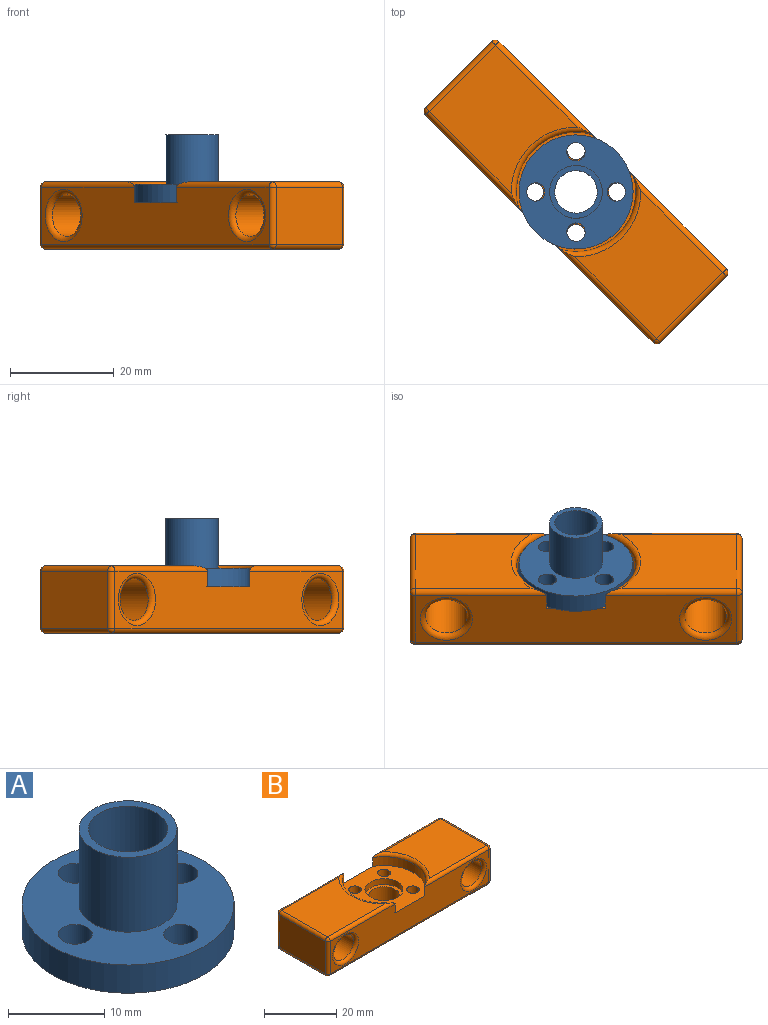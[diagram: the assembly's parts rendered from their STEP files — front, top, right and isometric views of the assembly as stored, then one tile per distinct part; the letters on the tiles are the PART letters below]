
ASSEMBLY  parts=2 mates=2
PART A: 12 faces, bbox 22x22x15.1 mm
  f0: cylinder r=1.77mm len=3.58mm, axis (0,0,-1), area 39.8mm2, adj f6,f7
  f1: cylinder r=1.77mm len=3.58mm, axis (0,0,-1), area 39.8mm2, adj f6,f7
  f2: cylinder r=1.77mm len=3.58mm, axis (0,0,-1), area 39.8mm2, adj f6,f7
  f3: cylinder r=1.77mm len=3.58mm, axis (0,0,-1), area 39.8mm2, adj f6,f7
  f4: cylinder r=4.1mm len=15.08mm, axis (0,0,-1), area 388.5mm2, adj f9,f11
  f5: cylinder r=11mm len=22mm, axis (0,0,-1), area 247.4mm2, adj f6,f7
  f6: plane 22x22mm, normal (0,0,1), area 259.5mm2, adj f0,f1,f2,f3,f5,f10
  f7: plane 22x22mm, normal (0,0,-1), area 245.7mm2, adj f0,f1,f2,f3,f5,f8
  f8: cylinder r=5.5mm len=11mm, axis (0,0,1), area 69.1mm2, adj f7,f9
  f9: plane 11x11mm, normal (0,0,-1), area 42.2mm2, adj f4,f8
  f10: cylinder r=5.08mm len=10.17mm, axis (0,0,-1), area 303.5mm2, adj f6,f11
  f11: plane 10.17x10.17mm, normal (0,0,1), area 28.4mm2, adj f4,f10
PART B: 75 faces, bbox 64x24.9x13 mm
  f0: cylinder r=4.25mm len=8.5mm, axis (0,0,1), area 186.9mm2, adj f4,f46
  f1: plane 22.33x18mm, normal (0,0,1), area 354.3mm2, adj f35,f36,f38,f40
  f2: plane 62x11mm, normal (0,-1,0), area 487.7mm2, adj f10,f11,f12,f22,f27,f32,f37,f40
  f3: plane 18x11mm, normal (-1,0,0), area 198mm2, adj f20,f21,f26,f27
  f4: plane 62x18mm, normal (0,0,-1), area 934.6mm2, adj f0,f25,f26,f31,f32,f47,f48,f49
  f5: plane 18x11mm, normal (1,0,0), area 198mm2, adj f30,f31,f36,f37
  f6: cylinder r=4.05mm len=18mm, axis (0,1,0), area 458mm2, adj f41,f43
  f7: plane 22.33x18mm, normal (0,0,1), area 354.3mm2, adj f17,f19,f21,f22
  f8: cylinder r=4.05mm len=18mm, axis (0,1,0), area 458mm2, adj f42,f44
  f9: plane 62x11mm, normal (0,1,0), area 487.7mm2, adj f10,f11,f12,f17,f20,f25,f30,f35
  f10: cylinder r=11.5mm len=20mm, axis (0,0,1), area 72.7mm2, adj f2,f9,f12,f38
  f11: cylinder r=11.5mm len=20mm, axis (0,0,1), area 72.7mm2, adj f2,f9,f12,f19
  f12: plane 23x20mm, normal (0,0,1), area 267.4mm2, adj f2,f9,f10,f11,f13,f14,f15,f16
  f13: cylinder r=1.75mm len=6mm, axis (0,0,1), area 66mm2, adj f12,f60
  f14: cylinder r=1.75mm len=6mm, axis (0,0,1), area 66mm2, adj f12,f74
  f15: cylinder r=1.75mm len=6mm, axis (0,0,1), area 66mm2, adj f12,f67
  f16: cylinder r=1.75mm len=6mm, axis (0,0,1), area 66mm2, adj f12,f53
  f17: cylinder r=1mm len=25.32mm, axis (-1,0,0), area 37.9mm2, adj f7,f9,f18,f19
  f18: sphere r=1mm, area 1.6mm2, adj f17,f20,f21
  f19: torus R=12.5mm, axis (0,0,1), area 35.5mm2, adj f7,f11,f17,f22
  f20: cylinder r=1mm len=11mm, axis (0,0,-1), area 17.3mm2, adj f3,f9,f18,f23
  f21: cylinder r=1mm len=18mm, axis (0,1,0), area 28.3mm2, adj f3,f7,f18,f24
  f22: cylinder r=1mm len=25.32mm, axis (1,0,0), area 37.9mm2, adj f2,f7,f19,f24
  f23: sphere r=1mm, area 1.6mm2, adj f20,f25,f26
  f24: sphere r=1mm, area 1.6mm2, adj f21,f22,f27
  f25: cylinder r=1mm len=62mm, axis (1,0,0), area 97.3mm2, adj f4,f9,f23,f28,f65,f66,f72,f73
  f26: cylinder r=1mm len=18mm, axis (0,-1,0), area 28.3mm2, adj f3,f4,f23,f29
  f27: cylinder r=1mm len=11mm, axis (0,0,1), area 17.3mm2, adj f2,f3,f24,f29
  f28: sphere r=1mm, area 1.6mm2, adj f25,f30,f31
  f29: sphere r=1mm, area 1.6mm2, adj f26,f27,f32
  f30: cylinder r=1mm len=11mm, axis (0,0,1), area 17.3mm2, adj f5,f9,f28,f33
  f31: cylinder r=1mm len=18mm, axis (0,1,0), area 28.3mm2, adj f4,f5,f28,f34
  f32: cylinder r=1mm len=62mm, axis (-1,0,0), area 97.3mm2, adj f2,f4,f29,f34,f51,f52,f58,f59
  f33: sphere r=1mm, area 1.6mm2, adj f30,f35,f36
  f34: sphere r=1mm, area 1.6mm2, adj f31,f32,f37
  f35: cylinder r=1mm len=25.32mm, axis (-1,0,0), area 37.9mm2, adj f1,f9,f33,f38
  f36: cylinder r=1mm len=18mm, axis (0,-1,0), area 28.3mm2, adj f1,f5,f33,f39
  f37: cylinder r=1mm len=11mm, axis (0,0,-1), area 17.3mm2, adj f2,f5,f34,f39
  f38: torus R=12.5mm, axis (0,0,1), area 35.5mm2, adj f1,f10,f35,f40
  f39: sphere r=1mm, area 1.6mm2, adj f36,f37,f40
  f40: cylinder r=1mm len=25.32mm, axis (1,0,0), area 37.9mm2, adj f1,f2,f38,f39
  f41: torus R=5.05mm, axis (0,-1,0), area 43.6mm2, adj f6,f9
  f42: torus R=5.05mm, axis (0,-1,0), area 43.6mm2, adj f8,f9
  f43: torus R=5.05mm, axis (0,-1,0), area 43.6mm2, adj f2,f6
  f44: torus R=5.05mm, axis (0,-1,0), area 43.6mm2, adj f2,f8
  f45: cylinder r=5.25mm len=10.5mm, axis (0,0,1), area 66mm2, adj f12,f46
  f46: plane 10.5x10.5mm, normal (0,0,1), area 29.8mm2, adj f0,f45
  f47: plane 3x3mm, normal (-0.5,-0.87,0), area 10.4mm2, adj f4,f48,f50,f53
  f48: plane 3x3mm, normal (0.5,-0.87,0), area 10.4mm2, adj f4,f47,f49,f53
  f49: plane 3.46x3mm, normal (1,0,0), area 10.4mm2, adj f4,f48,f51,f53
  f50: plane 3.46x3mm, normal (-1,0,0), area 10.4mm2, adj f4,f47,f52,f53
  f51: plane 3x3mm, normal (0.5,0.87,0), area 10.4mm2, adj f4,f32,f49,f52,f53
  f52: plane 3x3mm, normal (-0.5,0.87,0), area 10.4mm2, adj f4,f32,f50,f51,f53
  f53: plane 6.93x6mm, normal (0,0,-1), area 21.6mm2, adj f16,f47,f48,f49,f50,f51,f52
  f54: plane 3x3mm, normal (0.5,-0.87,0), area 10.4mm2, adj f4,f55,f57,f60
  f55: plane 3.46x3mm, normal (1,0,0), area 10.4mm2, adj f4,f54,f58,f60
  f56: plane 3.46x3mm, normal (-1,0,0), area 10.4mm2, adj f4,f57,f59,f60
  f57: plane 3x3mm, normal (-0.5,-0.87,0), area 10.4mm2, adj f4,f54,f56,f60
  f58: plane 3x3mm, normal (0.5,0.87,0), area 10.4mm2, adj f4,f32,f55,f59,f60
  f59: plane 3x3mm, normal (-0.5,0.87,0), area 10.4mm2, adj f4,f32,f56,f58,f60
  f60: plane 6.93x6mm, normal (0,0,-1), area 21.6mm2, adj f13,f54,f55,f56,f57,f58,f59
  f61: plane 3x3mm, normal (0.5,0.87,0), area 10.4mm2, adj f4,f62,f64,f67
  f62: plane 3x3mm, normal (-0.5,0.87,0), area 10.4mm2, adj f4,f61,f63,f67
  f63: plane 3.46x3mm, normal (-1,0,0), area 10.4mm2, adj f4,f62,f65,f67
  f64: plane 3.46x3mm, normal (1,0,0), area 10.4mm2, adj f4,f61,f66,f67
  f65: plane 3x3mm, normal (-0.5,-0.87,0), area 10.4mm2, adj f4,f25,f63,f66,f67
  f66: plane 3x3mm, normal (0.5,-0.87,0), area 10.4mm2, adj f4,f25,f64,f65,f67
  f67: plane 6.93x6mm, normal (0,0,-1), area 21.6mm2, adj f15,f61,f62,f63,f64,f65,f66
  f68: plane 3x3mm, normal (-0.5,0.87,0), area 10.4mm2, adj f4,f69,f71,f74
  f69: plane 3.46x3mm, normal (-1,0,0), area 10.4mm2, adj f4,f68,f72,f74
  f70: plane 3.46x3mm, normal (1,0,0), area 10.4mm2, adj f4,f71,f73,f74
  f71: plane 3x3mm, normal (0.5,0.87,0), area 10.4mm2, adj f4,f68,f70,f74
  f72: plane 3x3mm, normal (-0.5,-0.87,0), area 10.4mm2, adj f4,f25,f69,f73,f74
  f73: plane 3x3mm, normal (0.5,-0.87,0), area 10.4mm2, adj f4,f25,f70,f72,f74
  f74: plane 6.93x6mm, normal (0,0,-1), area 21.6mm2, adj f14,f68,f69,f70,f71,f72,f73
PLACE A t=(-26.47,-48.09,-35.53)mm
PLACE B rot(axis=(0,0,-1),45deg) t=(15.4,-19.25,13.02)mm
MATE revolute A.f2 <-> B.f13  axis (0,0,-1) through (-26.47,-55.84,-35.53)mm
MATE revolute A.f0 <-> B.f15  axis (0,0,-1) through (-26.47,-40.34,-35.53)mm
